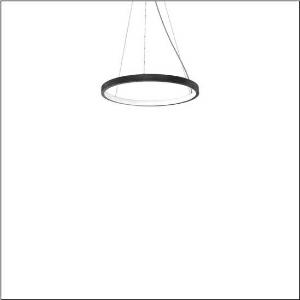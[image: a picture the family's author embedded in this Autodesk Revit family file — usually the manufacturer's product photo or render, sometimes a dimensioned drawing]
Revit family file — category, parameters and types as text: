
# Revit family: silica_r__21_ring-i_5pjbi1d1104a_8c46
name_source: partatom
category: Lighting Fixtures
units: mm (PartAtom-declared; Revit-internal decimal feet)

## family parameters
Cut with Voids When Loaded = No
Host = Face
Light Source = No
Part Type = Normal
Room Calculation Point = No
Round Connector Dimension = Use Diameter
Shared = No

## types (1)
- Silica® 21 Ring-I (1 x LED, 3430 lm, 60 W, 3000K)
    Apparent Load = 60 VA
    CIE Flux Codes = 22 48 76 50 101
    Color Rendering = 80
    Color Temperature = 3000K
    Default Elevation = 1800 mm
    Description = Silica® 21 Ring-I, suspended luminaire, of PMMA, frosted, light emission: inner ring side luminous distribution, primary light characteristic: symmetric, installation type: suspended mounting, LED, rated luminous flux: 3.430lm, luminous efficacy: 57lm/W, light colour: 830, colour temperature: 3000K, control gear: DALI 2, with terminal, 5-pole, mains connection: 230V, AC/DC, 0/50..60Hz, rated input power: 60W, housing, of extruded aluminium section, jet black (RAL 9005), diameter: 610mm, ceiling canopy, jet black (RAL 9005), protection rating (lamp compartment): IP40, insulation class (complete): insulation class I (protective earthing), certification: CE, impact resistance: IK02, permissible operating ambient temperature: 0..+35°C, packaging unit: 1 piece
    Height = 48 mm  [stored 0.15748 ft]
    Lamp = 1 x LED
    Lamp Light Flux = 3430 lm
    Lamp Power = 60 W
    Lamp count = 1
    Length = 610 mm
    Luminous efficacy = 57 lm/W
    Manufacturer = Siteco
    ModVariant = No
    Model = 5PJBI1D1104A
    Mounting Place = Ceiling
    Mounting Type = Pendant
    Number of Poles = 1
    OnlyDefault = Yes
    Power Factor = 1
    Product Name = Silica® 21 Ring-I
    Product group = suspended luminaire
    ProductGroupID = 905
    Protection Class = Protection class I
    Protection Degree = IP 40
    RLX_Detail_Level = 1
    RLX_Emergency_Light_Flux = 0 lm
    RLX_Emergency_Type = 0
    RLX_Emergency_Type_DB = No
    RlxData = <blob elided: 12369 chars, md5=e3d479e2>
    Socket = socket
    Standby Power = 0 W
    System Light Flux = 3430 lm
    System Power = 60 W
    Type Comments = Product without accessories
    Type Image = l_1258361.jpg
    URL = http://relux.com
    VarID = ---
    Voltage = 0 V
    Weight = 0.00 kg
    Width = 0 mm  [stored 0 ft]

note: [stored X ft] marks values corroborated as IEEE doubles in the binary element streams (Revit-internal decimal feet)

## geometry (parser evidence)
native form markers: Sweep x12
no freeform markers — native parametric forms only
